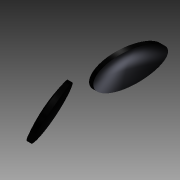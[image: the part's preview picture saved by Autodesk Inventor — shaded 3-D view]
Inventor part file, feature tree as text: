
AUTODESK INVENTOR PART (.ipt)
format: ipt  version: 2015 (Build 190159000, 159)  size: 120,832 bytes
history: native  units: in
note: dims shown in document units (in); Inventor stores cm internally (conversion verified against a paired STEP export)
features: sketch x4, reference x4, revolve x2, plane x1, extrude x1
ambient origin geometry x8: Origin, YZ Plane, XZ Plane, XY Plane, X Axis, Y Axis, Z Axis, Center Point
bodies: Solid1 (feature_tree)
feature tree (12):
  sketch  "Sketch1"  dims[d1=0.2in d2=0.2in]
  plane  "Work Plane1"
  extrude  "Extrusion1"  Depth=0.2in
  revolve  "Revolution1"  [1 undecoded]
  revolve  "Revolution2"  [1 undecoded]
  reference  "Reference1"
  sketch  "Sketch2"  dims[d3=0.35in d4=0.2in d5=0.0in]
  reference  "Reference2"
  reference  "Reference3"
  sketch  "Sketch3"  dims[d6=90.0deg d7=0.02in]
  reference  "Reference4"
  sketch  "Sketch4"  dims[d8=0.015in d9=90.0deg]
note: 2 required parameter values undecoded (feature->parameter linkage not recoverable at this tier; creation-order binding heuristic only, values carry confidence <= 0.55)
